# Revit family: WMH31017HW-005c_Cooking_MHC
name_source: partatom
category: Specialty Equipment
units: mm (PartAtom-declared; Revit-internal decimal feet)

## family parameters
Always vertical = Yes
Cut with Voids When Loaded = No
Enable Cutting in Views = No
Maintain Annotation Orientation = No
Part Type = Normal
Room Calculation Point = No
Round Connector Dimension = Use Diameter
Shared = No
Work Plane-Based = No

## types (1)
- WMH31017HW
    Accent Material = ARCAT - Metal - Aluminum
    Amps = 16 A
    Apparent Load = 0 VA
    Body Material = ARCAT - Metal - Steel - White
    CW size = 0"
    Clearance Material = ARCAT - Clearance
    Default Elevation = 0"
    Depth = 15 9/16"
    Description = Whirlpool® 1.7 cu. ft. Microwave Hood Combination with Electronic Touch Controls
    Display Material = ARCAT - Metal - Steel - White
    Door Material = ARCAT - Metal - Steel - White
    Drain size = 0"
    Exhaust size = 0"
    Family Name = Microwave Hood Combination
    Glass Material = ARCAT - Glass - Tempered - Black
    HW size = 0"
    Handle Material = ARCAT - Metal - Steel - White
    Height = 17 1/8"
    Installation-Fabrication = https://www.whirlpool.com
    Manufacturer = Whirlpool
    Model = WMH31017HW
    Product Data = https://www.whirlpool.com
    Sales Information = https://www.whirlpool.com
    URL = https://www.whirlpool.com
    Voltage = 120 V
    Warranty Duration (Years) = One year limited
    Width = 29 15/16"

## geometry (parser evidence)
native form markers: Sweep x1
no freeform markers — native parametric forms only
